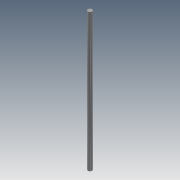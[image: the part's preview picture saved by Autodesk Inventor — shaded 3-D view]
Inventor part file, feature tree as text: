
AUTODESK INVENTOR PART (.ipt)
format: ipt  version: 2015 (Build 190159000, 159)  size: 70,656 bytes
history: native  units: mm
features: sketch x3, extrude x1
ambient origin geometry x8: Origin, YZ Plane, XZ Plane, XY Plane, X Axis, Y Axis, Z Axis, Center Point
bodies: Solid1 (feature_tree)
feature tree (4):
  sketch  "Sketch1"  dims[d1=6.0mm d2=200.0mm d3=0.0mm]
  sketch  "Sketch2"
  extrude  "Extrusion1"  Depth=200.0mm TaperAngle=0.0deg
  sketch  "Sketch3"
